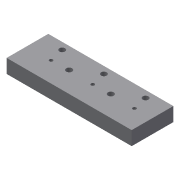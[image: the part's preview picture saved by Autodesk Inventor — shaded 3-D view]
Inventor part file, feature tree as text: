
AUTODESK INVENTOR PART (.ipt)
format: ipt  version: 2013 (Build 170138000, 138)  size: 144,896 bytes
history: native  units: in
note: dims shown in document units (in); Inventor stores cm internally (conversion verified against a paired STEP export)
features: extrude x6, sketch x6
ambient origin geometry x8: Origin, YZ Plane, XZ Plane, XY Plane, X Axis, Y Axis, Z Axis, Center Point
bodies: Solid1 (feature_tree)
feature tree (12):
  extrude  "Extrusion1"  Depth=1.1811in
  extrude  "Extrusion2"  Depth=0.1614in
  extrude  "Extrusion4"  Depth=0.1614in
  extrude  "Extrusion5"  Depth=0.1969in
  extrude  "Extrusion6"  Depth=0.5906in
  extrude  "Extrusion7"  Depth=1.1811in
  sketch  "Sketch1"  dims[d0=3.5433in d5=1.1811in]
  sketch  "Sketch2"  dims[d6=0.3937in d7=0.0in d8=0.1614in]
  sketch  "Sketch4"  dims[d10=0.1614in d11=0.1614in]
  sketch  "Sketch5"  dims[d12=0.1969in d13=0.1969in]
  sketch  "Sketch6"  dims[d14=0.1969in d15=0.5906in]
  sketch  "Sketch7"  dims[d16=1.1811in d17=1.1811in d18=0.3937in d19=0.0in d26=0.2756in d28=0.2756in d29=0.2756in d30=0.1772in d31=0.0in d32=0.1654in d34=0.1654in d35=1.1811in d36=1.1811in d37=0.5906in d38=0.5906in d39=0.3937in d40=0.0in d41=0.2756in d43=0.2756in d44=0.1772in d45=0.0in d46=0.0984in d48=0.0984in d49=0.0984in d50=0.4921in d51=0.5709in d52=1.1811in d53=1.1811in d54=0.5709in d55=0.5709in d56=0.7874in d57=0.0in]
